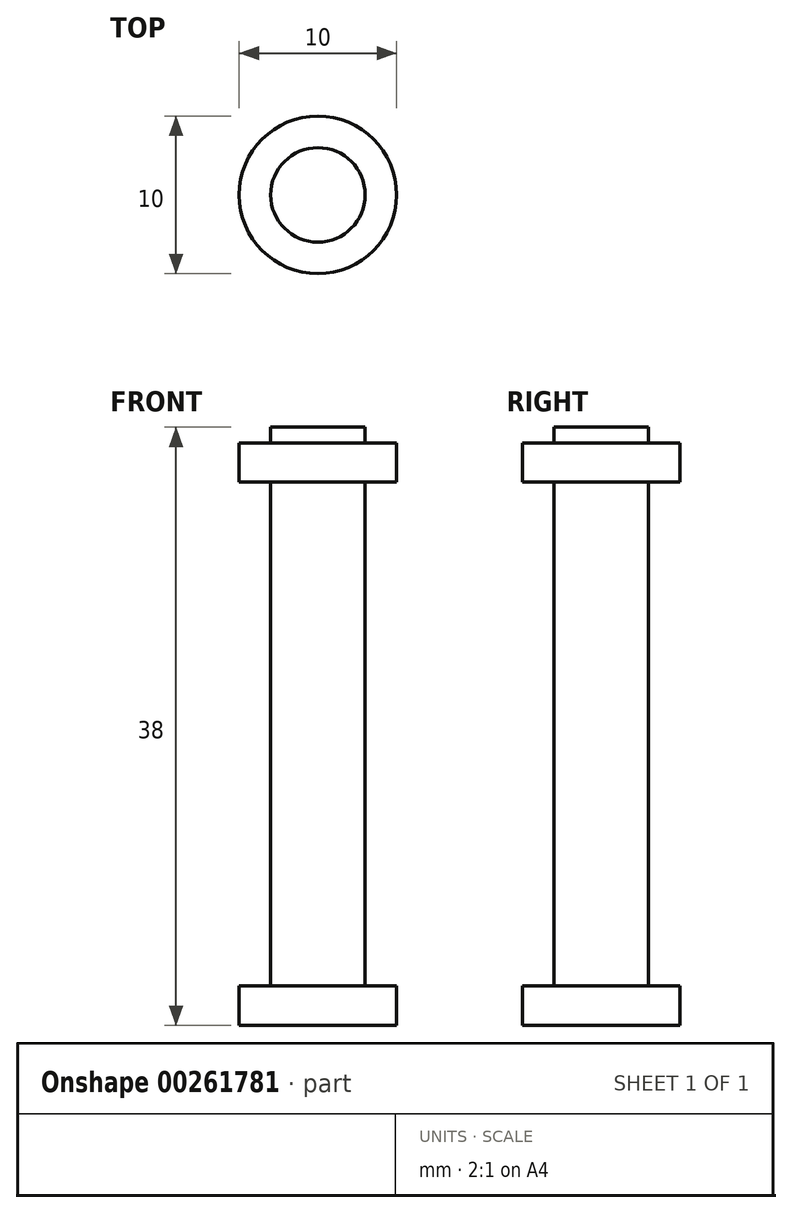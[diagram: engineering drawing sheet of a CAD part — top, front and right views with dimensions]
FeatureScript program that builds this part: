
annotation { "Feature Type Name" : "Feature", "Feature Type Description" : "" }
export const myFeature = defineFeature(function(context is Context, id is Id, definition is map)
    precondition{}
    {
        {
            var Q0;
            Q0=qCreatedBy(makeId("Front.planeOp"),FACE);
            var sketch = newSketch(context, id + "F0", { "sketchPlane" : qUnion([Q0])});
            skLineSegment(sketch, "E0", {"start": v(-3, 16) * mm, "end": v(-3, -16) * mm});
            skLineSegment(sketch, "E1", {"start": v(-3, 16) * mm, "end": v(0, 16) * mm});
            skLineSegment(sketch, "E2", {"start": v(-3, -16) * mm, "end": v(0, -16) * mm});
            skLineSegment(sketch, "E3", {"start": v(-3, 16) * mm, "end": v(-5, 16) * mm});
            skLineSegment(sketch, "E4", {"start": v(-5, 16) * mm, "end": v(-5, 18.5) * mm});
            skLineSegment(sketch, "E5", {"start": v(-5, 18.5) * mm, "end": v(0, 18.5) * mm});
            skLineSegment(sketch, "E6.MirrorCS", {"start": v(-5, -18.5) * mm, "end": v(0, -18.5) * mm});
            skLineSegment(sketch, "E7.MirrorCS", {"start": v(-5, -16) * mm, "end": v(-5, -18.5) * mm});
            skLineSegment(sketch, "E8.MirrorCS", {"start": v(-3, -16) * mm, "end": v(-5, -16) * mm});
            skLineSegment(sketch, "E9", {"start": v(-3, 18.5) * mm, "end": v(-3, 19.5) * mm});
            skLineSegment(sketch, "E10", {"start": v(-3, 19.5) * mm, "end": v(0, 19.5) * mm});
            skLineSegment(sketch, "E11", {"start": v(0, 19.5) * mm, "end": v(0, -18.5) * mm});
            skSolve(sketch);
        }
        {
            var Q0;
            Q0 = qSketchRegion(id + "F0", true);
            var Q1;
            Q1=sQuery(id+"F0.wireOp",EDGE,"E11");
            revolve(context, id + "F1", {"entities" : qUnion([Q0]), "axis" : qUnion([Q1]), "revolveType" : RevolveType.FULL});
        }
    });
